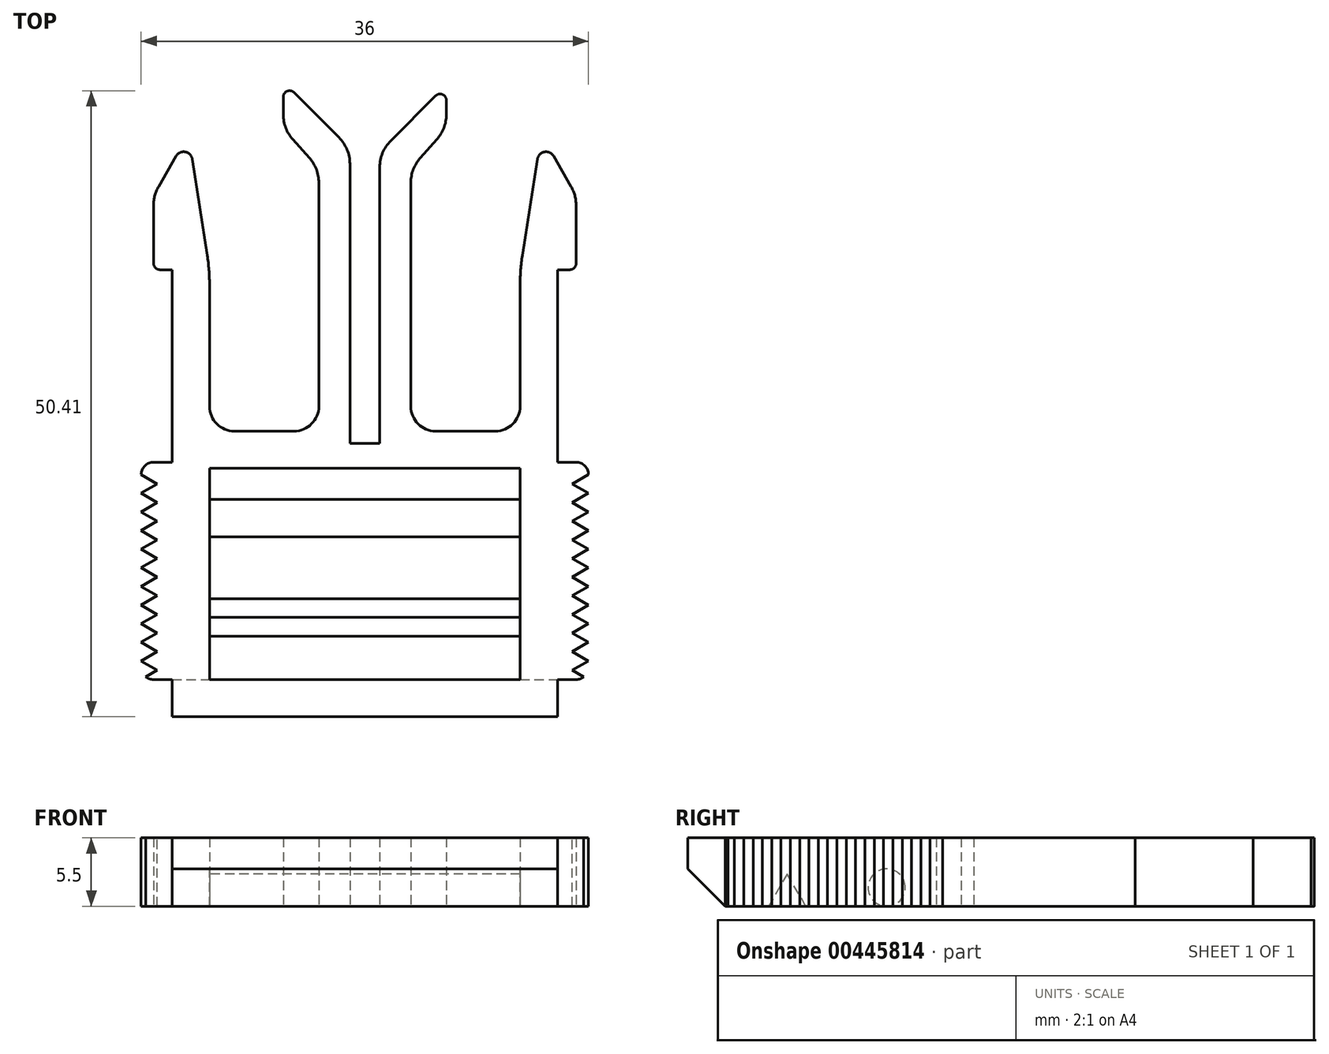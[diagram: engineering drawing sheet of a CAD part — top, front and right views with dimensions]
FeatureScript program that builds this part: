
annotation { "Feature Type Name" : "Feature", "Feature Type Description" : "" }
export const myFeature = defineFeature(function(context is Context, id is Id, definition is map)
    precondition{}
    {
        {
            var Q0;
            Q0=qCreatedBy(makeId("Top.planeOp"),FACE);
            var sketch = newSketch(context, id + "F0", { "sketchPlane" : qUnion([Q0])});
            skLineSegment(sketch, "E0.top", {"start": v(15.5, -24.35) * mm, "end": v(-15.5, -24.35) * mm});
            skPoint(sketch, "E0.middle", {"position": v(0, 0) * mm});
            skLineSegment(sketch, "E1.bottom", {"start": v(12.5, -4.35) * mm, "end": v(-12.5, -4.35) * mm});
            skLineSegment(sketch, "E1.top", {"start": v(12.5, -21.35) * mm, "end": v(-12.5, -21.35) * mm});
            skLineSegment(sketch, "E1.left", {"start": v(12.5, -4.35) * mm, "end": v(12.5, -21.35) * mm});
            skLineSegment(sketch, "E1.right", {"start": v(-12.5, -4.35) * mm, "end": v(-12.5, -21.35) * mm});
            skPoint(sketch, "E1.middle", {"position": v(0, -12.85) * mm});
            skLineSegment(sketch, "E2", {"start": v(15.18, 20.8) * mm, "end": v(16.6, 18.34) * mm});
            skLineSegment(sketch, "E3", {"start": v(17, 16.84) * mm, "end": v(17, 12.15) * mm});
            skLineSegment(sketch, "E4", {"start": v(16.5, 11.65) * mm, "end": v(15.5, 11.65) * mm});
            skLineSegment(sketch, "E5", {"start": v(0, -4.35) * mm, "end": v(0, 27.9) * mm, "construction": true});
            skLineSegment(sketch, "E6", {"start": v(-10.5, -1.35) * mm, "end": v(-5.7, -1.35) * mm});
            skLineSegment(sketch, "E7.trimOffspring", {"start": v(15.5, 11.65) * mm, "end": v(15.5, -24.35) * mm});
            skLineSegment(sketch, "E8", {"start": v(12.5, 10.49) * mm, "end": v(12.5, 0.65) * mm});
            skLineSegment(sketch, "E9.0", {"start": v(-3.7, 0.65) * mm, "end": v(-3.7, 18.65) * mm});
            skLineSegment(sketch, "E10.0", {"start": v(3.7, 0.65) * mm, "end": v(3.7, 18.65) * mm});
            skLineSegment(sketch, "E11", {"start": v(13.89, 20.55) * mm, "end": v(12.68, 12.8) * mm});
            skPoint(sketch, "E12.visualSharp", {"position": v(12.5, 11.65) * mm});
            skArc(sketch, "E12.filletArc", {"start": v(12.68, 12.8) * mm, "mid": v(12.54, 11.64) * mm, "end": v(12.5, 10.49) * mm});
            skLineSegment(sketch, "E13.trimOffspring", {"start": v(5.7, -1.35) * mm, "end": v(10.5, -1.35) * mm});
            skPoint(sketch, "E14.orphan", {"position": v(13.51, 18.14) * mm});
            skPoint(sketch, "E15.orphan", {"position": v(16.29, 18.88) * mm});
            skPoint(sketch, "E16.orphan", {"position": v(15.5, -1.35) * mm});
            skPoint(sketch, "E17.visualSharp", {"position": v(14.2, 22.51) * mm});
            skArc(sketch, "E17.filletArc", {"start": v(15.18, 20.8) * mm, "mid": v(14.45, 21.13) * mm, "end": v(13.89, 20.55) * mm});
            skArc(sketch, "E18.MirrorCS", {"start": v(-15.18, 20.8) * mm, "mid": v(-14.45, 21.13) * mm, "end": v(-13.89, 20.55) * mm});
            skLineSegment(sketch, "E19.MirrorCS", {"start": v(-15.18, 20.8) * mm, "end": v(-16.6, 18.34) * mm});
            skLineSegment(sketch, "E20.MirrorCS", {"start": v(-16.5, 11.65) * mm, "end": v(-15.5, 11.65) * mm});
            skPoint(sketch, "E21.MirrorP", {"position": v(-13.51, 18.14) * mm});
            skPoint(sketch, "E22.MirrorP", {"position": v(-12.5, 11.65) * mm});
            skArc(sketch, "E23.MirrorCS", {"start": v(-12.68, 12.8) * mm, "mid": v(-12.54, 11.64) * mm, "end": v(-12.5, 10.49) * mm});
            skPoint(sketch, "E24.MirrorP", {"position": v(-14.2, 22.51) * mm});
            skPoint(sketch, "E25.MirrorP", {"position": v(-16.29, 18.88) * mm});
            skLineSegment(sketch, "E26.MirrorCS", {"start": v(-17, 16.84) * mm, "end": v(-17, 12.15) * mm});
            skLineSegment(sketch, "E27.MirrorCS", {"start": v(-13.89, 20.55) * mm, "end": v(-12.68, 12.8) * mm});
            skLineSegment(sketch, "E28.MirrorCS", {"start": v(-15.5, 11.65) * mm, "end": v(-15.5, -24.35) * mm});
            skLineSegment(sketch, "E29.MirrorCS", {"start": v(-12.5, 10.49) * mm, "end": v(-12.5, 0.65) * mm});
            skLineSegment(sketch, "E30.0", {"start": v(1.2, -2.35) * mm, "end": v(1.2, 19.9) * mm});
            skLineSegment(sketch, "E31.0", {"start": v(-1.2, -2.35) * mm, "end": v(-1.2, 20.17) * mm});
            skLineSegment(sketch, "E32", {"start": v(5.7, 25.65) * mm, "end": v(2.08, 22.03) * mm});
            skLineSegment(sketch, "E33", {"start": v(-5.7, 25.92) * mm, "end": v(-2.08, 22.29) * mm});
            skPoint(sketch, "E34.visualSharp", {"position": v(17, 17.65) * mm});
            skArc(sketch, "E34.filletArc", {"start": v(17, 16.84) * mm, "mid": v(16.9, 17.62) * mm, "end": v(16.6, 18.34) * mm});
            skPoint(sketch, "E35.visualSharp", {"position": v(-17, 17.65) * mm});
            skArc(sketch, "E35.filletArc", {"start": v(-16.6, 18.34) * mm, "mid": v(-16.9, 17.62) * mm, "end": v(-17, 16.84) * mm});
            skLineSegment(sketch, "E36", {"start": v(-1.2, -2.35) * mm, "end": v(1.2, -2.35) * mm});
            skPoint(sketch, "E37.orphan", {"position": v(1.2, 0.65) * mm});
            skPoint(sketch, "E38.orphan", {"position": v(-1.2, 0.65) * mm});
            skLineSegment(sketch, "E39", {"start": v(4.46, 20.65) * mm, "end": v(5.8, 22.14) * mm});
            skLineSegment(sketch, "E40", {"start": v(6.56, 24.14) * mm, "end": v(6.56, 25.3) * mm});
            skLineSegment(sketch, "E41.MirrorCS", {"start": v(-4.46, 20.65) * mm, "end": v(-5.8, 22.14) * mm});
            skLineSegment(sketch, "E42.MirrorCS", {"start": v(-6.56, 24.14) * mm, "end": v(-6.56, 25.56) * mm});
            skPoint(sketch, "E43.newPointB", {"position": v(6.56, 27.77) * mm});
            skArc(sketch, "E43.filletArc", {"start": v(6.56, 25.3) * mm, "mid": v(6.25, 25.76) * mm, "end": v(5.7, 25.65) * mm});
            skPoint(sketch, "E44.newPointB", {"position": v(-6.56, 27.77) * mm});
            skArc(sketch, "E44.filletArc", {"start": v(-5.7, 25.92) * mm, "mid": v(-6.25, 26.03) * mm, "end": v(-6.56, 25.56) * mm});
            skPoint(sketch, "E45.orphan", {"position": v(3.7, 23.65) * mm});
            skPoint(sketch, "E46.orphan", {"position": v(-3.7, 23.91) * mm});
            skPoint(sketch, "E47.visualSharp", {"position": v(3.7, 19.8) * mm});
            skArc(sketch, "E47.filletArc", {"start": v(4.46, 20.65) * mm, "mid": v(3.9, 19.72) * mm, "end": v(3.7, 18.65) * mm});
            skPoint(sketch, "E48.visualSharp", {"position": v(1.2, 21.15) * mm});
            skArc(sketch, "E48.filletArc", {"start": v(2.08, 22.03) * mm, "mid": v(1.43, 21.05) * mm, "end": v(1.2, 19.9) * mm});
            skPoint(sketch, "E49.visualSharp", {"position": v(-1.2, 21.41) * mm});
            skArc(sketch, "E49.filletArc", {"start": v(-1.2, 20.17) * mm, "mid": v(-1.43, 21.32) * mm, "end": v(-2.08, 22.29) * mm});
            skPoint(sketch, "E50.visualSharp", {"position": v(-3.7, 19.8) * mm});
            skArc(sketch, "E50.filletArc", {"start": v(-3.7, 18.65) * mm, "mid": v(-3.9, 19.72) * mm, "end": v(-4.46, 20.65) * mm});
            skPoint(sketch, "E51.visualSharp", {"position": v(6.56, 23) * mm});
            skArc(sketch, "E51.filletArc", {"start": v(5.8, 22.14) * mm, "mid": v(6.36, 23.07) * mm, "end": v(6.56, 24.14) * mm});
            skPoint(sketch, "E52.visualSharp", {"position": v(-6.56, 23) * mm});
            skArc(sketch, "E52.filletArc", {"start": v(-6.56, 24.14) * mm, "mid": v(-6.36, 23.07) * mm, "end": v(-5.8, 22.14) * mm});
            skPoint(sketch, "E53.visualSharp", {"position": v(12.5, -1.35) * mm});
            skArc(sketch, "E53.filletArc", {"start": v(10.5, -1.35) * mm, "mid": v(11.91, -0.77) * mm, "end": v(12.5, 0.65) * mm});
            skPoint(sketch, "E54.visualSharp", {"position": v(-12.5, -1.35) * mm});
            skArc(sketch, "E54.filletArc", {"start": v(-12.5, 0.65) * mm, "mid": v(-11.91, -0.77) * mm, "end": v(-10.5, -1.35) * mm});
            skPoint(sketch, "E55.visualSharp", {"position": v(-3.7, -1.35) * mm});
            skArc(sketch, "E55.filletArc", {"start": v(-5.7, -1.35) * mm, "mid": v(-4.29, -0.77) * mm, "end": v(-3.7, 0.65) * mm});
            skPoint(sketch, "E56.visualSharp", {"position": v(3.7, -1.35) * mm});
            skArc(sketch, "E56.filletArc", {"start": v(3.7, 0.65) * mm, "mid": v(4.29, -0.77) * mm, "end": v(5.7, -1.35) * mm});
            skPoint(sketch, "E57.visualSharp", {"position": v(17, 11.65) * mm});
            skArc(sketch, "E57.filletArc", {"start": v(16.5, 11.65) * mm, "mid": v(16.85, 11.8) * mm, "end": v(17, 12.15) * mm});
            skPoint(sketch, "E58.visualSharp", {"position": v(-17, 11.65) * mm});
            skArc(sketch, "E58.filletArc", {"start": v(-17, 12.15) * mm, "mid": v(-16.85, 11.8) * mm, "end": v(-16.5, 11.65) * mm});
            skSolve(sketch);
        }
        {
            var Q0;
            Q0=makeQuery(id+"F0.imprint","IMPRINT",FACE,{"disambiguationData":[TD([[makeQuery(id+"F0.imprint","IMPRINT",EDGE,{"derivedFrom":sQuery(id+"F0.wireOp",EDGE,"E0.top")}),-1.0]])]});
            extrude(context, id + "F1", {"entities" : qUnion([Q0]), "depth" : 5.5 * mm});
        }
        {
            var Q0;
            Q0=makeQuery(id+"F1.opExtrude","SWEPT_FACE",FACE,{"disambiguationData":[OSD([sQuery(id+"F0.wireOp",EDGE,"E1.right")])]});
            var sketch = newSketch(context, id + "F2", { "sketchPlane" : qUnion([Q0])});
            skLineSegment(sketch, "E59", {"start": v(-16.35, 2.6) * mm, "end": v(-17.85, 0) * mm});
            skLineSegment(sketch, "E60", {"start": v(-17.85, 0) * mm, "end": v(-14.85, 0) * mm});
            skLineSegment(sketch, "E61", {"start": v(-14.85, 0) * mm, "end": v(-16.35, 2.6) * mm});
            skCircle(sketch, "E62", {"center": v(-8.35, 1.5) * mm, "radius": 1.5 * mm});
            skPoint(sketch, "E62.centerSnap0", {"position": v(-4.35, 2.75) * mm});
            skSolve(sketch);
        }
        {
            var Q0;
            Q0=makeQuery(id+"F2.imprint","IMPRINT",FACE,{"disambiguationData":[TD([[makeQuery(id+"F2.imprint","IMPRINT",EDGE,{"derivedFrom":sQuery(id+"F2.wireOp",EDGE,"E59")}),1.0]])]});
            var Q1;
            Q1=makeQuery(id+"F2.imprint","IMPRINT",FACE,{"disambiguationData":[TD([[makeQuery(id+"F2.imprint","IMPRINT",EDGE,{"derivedFrom":sQuery(id+"F2.wireOp",EDGE,"E62")}),1.0]])]});
            extrude(context, id + "F3", {"entities" : qUnion([Q0, Q1]), "operationType" : NewBodyOperationType.ADD, "depth" : 25 * mm});
        }
        {
            var Q0;
            Q0=makeQuery(id+"F1.opExtrude","SWEPT_FACE",FACE,{"disambiguationData":[OSD([sQuery(id+"F0.wireOp",EDGE,"E7.trimOffspring")])]});
            var sketch = newSketch(context, id + "F4", { "sketchPlane" : qUnion([Q0])});
            skLineSegment(sketch, "E63", {"start": v(-21.35, 0) * mm, "end": v(-24.35, 3) * mm});
            skSolve(sketch);
        }
        {
            var Q0;
            {var subQ0=sQuery(id+"F4.wireOp",EDGE,"E63");Q0=makeQuery(id+"F4.imprint","IMPRINT",FACE,{"disambiguationData":[TD([[makeQuery(id+"F4.imprint","IMPRINT",EDGE,{"derivedFrom":subQ0}),1.0]])]});}
            var Q1;
            Q1=makeQuery(id+"F1.opExtrude","SWEPT_FACE",FACE,{"disambiguationData":[OSD([sQuery(id+"F0.wireOp",EDGE,"E1.right")])]});
            var Q2;
            Q2=makeQuery(id+"F1.opExtrude","SWEPT_FACE",FACE,{"disambiguationData":[OSD([sQuery(id+"F0.wireOp",EDGE,"E1.left")])]});
            extrude(context, id + "F5", {"entities" : qUnion([Q0]), "operationType" : NewBodyOperationType.REMOVE, "endBound" : BoundingType.THROUGH_ALL, "oppositeDirection" : true, "endBoundEntityFace" : qUnion([Q1]), "depth" : 25 * mm});
        }
        {
            var Q0;
            Q0=makeQuery(id+"F1.opExtrude","CAP_FACE",FACE,{"disambiguationData":[OSD([sQuery(id+"F0.wireOp",EDGE,"E0.top"),sQuery(id+"F0.wireOp",EDGE,"E1.bottom"),sQuery(id+"F0.wireOp",EDGE,"E1.top"),sQuery(id+"F0.wireOp",EDGE,"E1.left"),sQuery(id+"F0.wireOp",EDGE,"E1.right"),sQuery(id+"F0.wireOp",EDGE,"E2"),sQuery(id+"F0.wireOp",EDGE,"E3"),sQuery(id+"F0.wireOp",EDGE,"E4"),sQuery(id+"F0.wireOp",EDGE,"E6"),sQuery(id+"F0.wireOp",EDGE,"E7.trimOffspring"),sQuery(id+"F0.wireOp",EDGE,"E8"),sQuery(id+"F0.wireOp",EDGE,"E9.0"),sQuery(id+"F0.wireOp",EDGE,"E10.0"),sQuery(id+"F0.wireOp",EDGE,"E11"),sQuery(id+"F0.wireOp",EDGE,"E12.filletArc"),sQuery(id+"F0.wireOp",EDGE,"E13.trimOffspring"),sQuery(id+"F0.wireOp",EDGE,"E17.filletArc"),sQuery(id+"F0.wireOp",EDGE,"E18.MirrorCS"),sQuery(id+"F0.wireOp",EDGE,"E19.MirrorCS"),sQuery(id+"F0.wireOp",EDGE,"E20.MirrorCS"),sQuery(id+"F0.wireOp",EDGE,"E23.MirrorCS"),sQuery(id+"F0.wireOp",EDGE,"E26.MirrorCS"),sQuery(id+"F0.wireOp",EDGE,"E27.MirrorCS"),sQuery(id+"F0.wireOp",EDGE,"E28.MirrorCS"),sQuery(id+"F0.wireOp",EDGE,"E29.MirrorCS"),sQuery(id+"F0.wireOp",EDGE,"E30.0"),sQuery(id+"F0.wireOp",EDGE,"E31.0"),sQuery(id+"F0.wireOp",EDGE,"UTjdTIHE-D38J-cQlS-tRNC-KbjzHWpZoidh"),sQuery(id+"F0.wireOp",EDGE,"E32"),sQuery(id+"F0.wireOp",EDGE,"E33"),sQuery(id+"F0.wireOp",EDGE,"E34.filletArc"),sQuery(id+"F0.wireOp",EDGE,"E35.filletArc")])],"isStart":false});
            var sketch = newSketch(context, id + "F6", { "sketchPlane" : qUnion([Q0])});
            skLineSegment(sketch, "E64", {"start": v(15.5, -3.85) * mm, "end": v(17, -3.85) * mm});
            skLineSegment(sketch, "E65", {"start": v(18, -4.85) * mm, "end": v(18, -20.35) * mm});
            skLineSegment(sketch, "E66", {"start": v(17, -21.35) * mm, "end": v(15.5, -21.35) * mm});
            skPoint(sketch, "E67.visualSharp", {"position": v(18, -3.85) * mm});
            skArc(sketch, "E67.filletArc", {"start": v(18, -4.85) * mm, "mid": v(17.7, -4.15) * mm, "end": v(17, -3.85) * mm});
            skPoint(sketch, "E68.visualSharp", {"position": v(18, -21.35) * mm});
            skArc(sketch, "E68.filletArc", {"start": v(17, -21.35) * mm, "mid": v(17.7, -21.06) * mm, "end": v(18, -20.35) * mm});
            skLineSegment(sketch, "E69", {"start": v(15.5, -3.85) * mm, "end": v(15.5, -21.35) * mm});
            skSolve(sketch);
        }
        {
            var Q0;
            Q0=makeQuery(id+"F6.imprint","IMPRINT",FACE,{"disambiguationData":[TD([[makeQuery(id+"F6.imprint","IMPRINT",EDGE,{"derivedFrom":sQuery(id+"F6.wireOp",EDGE,"E64")}),-1.0]])]});
            var Q1;
            Q1=makeQuery(id+"F1.opExtrude","CAP_FACE",FACE,{"disambiguationData":[OSD([sQuery(id+"F0.wireOp",EDGE,"E0.top"),sQuery(id+"F0.wireOp",EDGE,"E1.bottom"),sQuery(id+"F0.wireOp",EDGE,"E1.top"),sQuery(id+"F0.wireOp",EDGE,"E1.left"),sQuery(id+"F0.wireOp",EDGE,"E1.right"),sQuery(id+"F0.wireOp",EDGE,"E2"),sQuery(id+"F0.wireOp",EDGE,"E3"),sQuery(id+"F0.wireOp",EDGE,"E4"),sQuery(id+"F0.wireOp",EDGE,"E6"),sQuery(id+"F0.wireOp",EDGE,"E7.trimOffspring"),sQuery(id+"F0.wireOp",EDGE,"E8"),sQuery(id+"F0.wireOp",EDGE,"E9.0"),sQuery(id+"F0.wireOp",EDGE,"E10.0"),sQuery(id+"F0.wireOp",EDGE,"E11"),sQuery(id+"F0.wireOp",EDGE,"E12.filletArc"),sQuery(id+"F0.wireOp",EDGE,"E13.trimOffspring"),sQuery(id+"F0.wireOp",EDGE,"E17.filletArc"),sQuery(id+"F0.wireOp",EDGE,"E18.MirrorCS"),sQuery(id+"F0.wireOp",EDGE,"E19.MirrorCS"),sQuery(id+"F0.wireOp",EDGE,"E20.MirrorCS"),sQuery(id+"F0.wireOp",EDGE,"E23.MirrorCS"),sQuery(id+"F0.wireOp",EDGE,"E26.MirrorCS"),sQuery(id+"F0.wireOp",EDGE,"E27.MirrorCS"),sQuery(id+"F0.wireOp",EDGE,"E28.MirrorCS"),sQuery(id+"F0.wireOp",EDGE,"E29.MirrorCS"),sQuery(id+"F0.wireOp",EDGE,"E30.0"),sQuery(id+"F0.wireOp",EDGE,"E31.0"),sQuery(id+"F0.wireOp",EDGE,"UTjdTIHE-D38J-cQlS-tRNC-KbjzHWpZoidh"),sQuery(id+"F0.wireOp",EDGE,"E32"),sQuery(id+"F0.wireOp",EDGE,"E33"),sQuery(id+"F0.wireOp",EDGE,"E34.filletArc"),sQuery(id+"F0.wireOp",EDGE,"E35.filletArc")])],"isStart":true});
            extrude(context, id + "F7", {"entities" : qUnion([Q0]), "endBound" : BoundingType.UP_TO_SURFACE, "oppositeDirection" : true, "endBoundEntityFace" : qUnion([Q1]), "depth" : 25 * mm});
        }
        {
            var Q0;
            Q0=makeQuery(id+"F7.opExtrude","CAP_FACE",FACE,{"disambiguationData":[OSD([sQuery(id+"F6.wireOp",EDGE,"E64"),sQuery(id+"F6.wireOp",EDGE,"E65"),sQuery(id+"F6.wireOp",EDGE,"E66"),sQuery(id+"F6.wireOp",EDGE,"E67.filletArc"),sQuery(id+"F6.wireOp",EDGE,"E68.filletArc"),sQuery(id+"F6.wireOp",EDGE,"E69")])],"isStart":true});
            var sketch = newSketch(context, id + "F8", { "sketchPlane" : qUnion([Q0])});
            skLineSegment(sketch, "E70", {"start": v(18, -4.85) * mm, "end": v(16.7, -5.6) * mm});
            skLineSegment(sketch, "E71", {"start": v(16.7, -5.6) * mm, "end": v(18, -6.35) * mm});
            skLineSegment(sketch, "E72", {"start": v(18, -6.35) * mm, "end": v(18, -4.85) * mm});
            skLineSegment(sketch, "E73.0.1.0", {"start": v(18, -7.85) * mm, "end": v(18, -6.35) * mm});
            skLineSegment(sketch, "E73.0.1.1", {"start": v(16.7, -7.1) * mm, "end": v(18, -7.85) * mm});
            skLineSegment(sketch, "E73.0.1.2", {"start": v(18, -6.35) * mm, "end": v(16.7, -7.1) * mm});
            skLineSegment(sketch, "E73.0.2.0", {"start": v(18, -9.35) * mm, "end": v(18, -7.85) * mm});
            skLineSegment(sketch, "E73.0.2.1", {"start": v(16.7, -8.6) * mm, "end": v(18, -9.35) * mm});
            skLineSegment(sketch, "E73.0.2.2", {"start": v(18, -7.85) * mm, "end": v(16.7, -8.6) * mm});
            skLineSegment(sketch, "E73.0.3.0", {"start": v(18, -10.85) * mm, "end": v(18, -9.35) * mm});
            skLineSegment(sketch, "E73.0.3.1", {"start": v(16.7, -10.1) * mm, "end": v(18, -10.85) * mm});
            skLineSegment(sketch, "E73.0.3.2", {"start": v(18, -9.35) * mm, "end": v(16.7, -10.1) * mm});
            skLineSegment(sketch, "E73.0.4.0", {"start": v(18, -12.35) * mm, "end": v(18, -10.85) * mm});
            skLineSegment(sketch, "E73.0.4.1", {"start": v(16.7, -11.6) * mm, "end": v(18, -12.35) * mm});
            skLineSegment(sketch, "E73.0.4.2", {"start": v(18, -10.85) * mm, "end": v(16.7, -11.6) * mm});
            skLineSegment(sketch, "E73.0.5.0", {"start": v(18, -13.85) * mm, "end": v(18, -12.35) * mm});
            skLineSegment(sketch, "E73.0.5.1", {"start": v(16.7, -13.1) * mm, "end": v(18, -13.85) * mm});
            skLineSegment(sketch, "E73.0.5.2", {"start": v(18, -12.35) * mm, "end": v(16.7, -13.1) * mm});
            skLineSegment(sketch, "E73.0.6.0", {"start": v(18, -15.35) * mm, "end": v(18, -13.85) * mm});
            skLineSegment(sketch, "E73.0.6.1", {"start": v(16.7, -14.6) * mm, "end": v(18, -15.35) * mm});
            skLineSegment(sketch, "E73.0.6.2", {"start": v(18, -13.85) * mm, "end": v(16.7, -14.6) * mm});
            skLineSegment(sketch, "E73.0.7.0", {"start": v(18, -16.85) * mm, "end": v(18, -15.35) * mm});
            skLineSegment(sketch, "E73.0.7.1", {"start": v(16.7, -16.1) * mm, "end": v(18, -16.85) * mm});
            skLineSegment(sketch, "E73.0.7.2", {"start": v(18, -15.35) * mm, "end": v(16.7, -16.1) * mm});
            skLineSegment(sketch, "E73.0.8.0", {"start": v(18, -18.35) * mm, "end": v(18, -16.85) * mm});
            skLineSegment(sketch, "E73.0.8.1", {"start": v(16.7, -17.6) * mm, "end": v(18, -18.35) * mm});
            skLineSegment(sketch, "E73.0.8.2", {"start": v(18, -16.85) * mm, "end": v(16.7, -17.6) * mm});
            skLineSegment(sketch, "E73.0.9.0", {"start": v(18, -19.85) * mm, "end": v(18, -18.35) * mm});
            skLineSegment(sketch, "E73.0.9.1", {"start": v(16.7, -19.1) * mm, "end": v(18, -19.85) * mm});
            skLineSegment(sketch, "E73.0.9.2", {"start": v(18, -18.35) * mm, "end": v(16.7, -19.1) * mm});
            skLineSegment(sketch, "E73.0.10.0", {"start": v(18, -21.35) * mm, "end": v(18, -19.85) * mm});
            skLineSegment(sketch, "E73.0.10.1", {"start": v(16.7, -20.6) * mm, "end": v(18, -21.35) * mm});
            skLineSegment(sketch, "E73.0.10.2", {"start": v(18, -19.85) * mm, "end": v(16.7, -20.6) * mm});
            skLineSegment(sketch, "E73.direction1", {"start": v(18, -6.35) * mm, "end": v(36.9, -6.35) * mm, "construction": true});
            skLineSegment(sketch, "E73.direction2", {"start": v(18, -6.35) * mm, "end": v(18, -7.85) * mm, "construction": true});
            skLineSegment(sketch, "E74", {"start": v(0, 0) * mm, "end": v(0, -26.7) * mm, "construction": true});
            skSolve(sketch);
        }
        {
            var Q0;
            Q0=qSketchRegion(id+"F8",true);
            extrude(context, id + "F9", {"entities" : qUnion([Q0]), "operationType" : NewBodyOperationType.REMOVE, "endBound" : BoundingType.THROUGH_ALL, "oppositeDirection" : true, "depth" : 25 * mm});
        }
        {
            var Q0;
            Q0=makeQuery(id+"F1.opExtrude","SWEPT_FACE",FACE,{"disambiguationData":[OSD([sQuery(id+"F0.wireOp",EDGE,"E7.trimOffspring")])]});
            var Q1;
            Q1=makeQuery(id+"F1.opExtrude","SWEPT_FACE",FACE,{"disambiguationData":[OSD([sQuery(id+"F0.wireOp",EDGE,"E28.MirrorCS")])]});
            cPlane(context, id + "F10", {"entities" : qUnion([Q0, Q1]), "cplaneType" : CPlaneType.MID_PLANE, "offset" : 150 * mm, "width" : 150 * mm, "height" : 150 * mm});
        }
        {
            var Q0;
            Q0=makeQuery(id+"F7.opExtrude","SWEPT_BODY",BODY,{"disambiguationData":[OSD([sQuery(id+"F6.wireOp",EDGE,"E64"),sQuery(id+"F6.wireOp",EDGE,"E65"),sQuery(id+"F6.wireOp",EDGE,"E66"),sQuery(id+"F6.wireOp",EDGE,"E67.filletArc"),sQuery(id+"F6.wireOp",EDGE,"E68.filletArc"),sQuery(id+"F6.wireOp",EDGE,"E69")])]});
            var Q1;
            Q1=qCreatedBy(id+"F10.planeOp",FACE);
            mirror(context, id + "F11", {"operationType" : NewBodyOperationType.ADD, "entities" : qUnion([Q0]), "mirrorPlane" : qUnion([Q1])});
        }
    });
